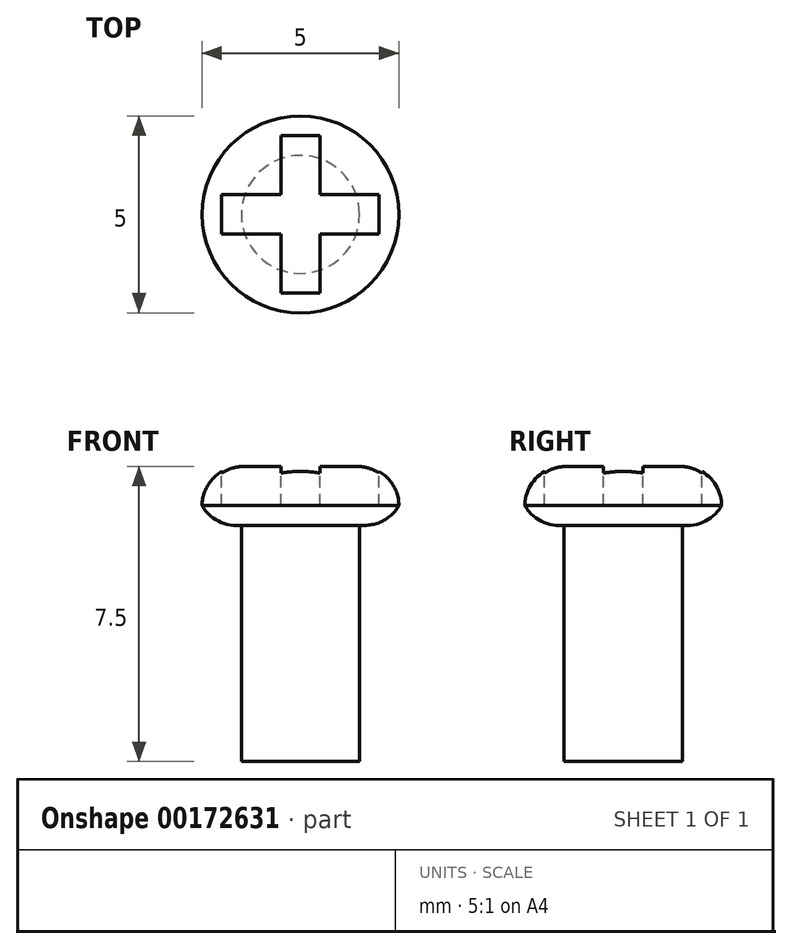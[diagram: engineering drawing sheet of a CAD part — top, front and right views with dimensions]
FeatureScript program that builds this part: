
annotation { "Feature Type Name" : "Feature", "Feature Type Description" : "" }
export const myFeature = defineFeature(function(context is Context, id is Id, definition is map)
    precondition{}
    {
        {
            var Q0;
            Q0=qCreatedBy(makeId("Top.planeOp"),FACE);
            var sketch = newSketch(context, id + "F0", { "sketchPlane" : qUnion([Q0])});
            skCircle(sketch, "E0", {"center": v(0, 0) * mm, "radius": 1.5 * mm});
            skSolve(sketch);
        }
        {
            var Q0;
            Q0 = qSketchRegion(id + "F0", true);
            extrude(context, id + "F1", {"entities" : qUnion([Q0]), "depth" : 6 * mm});
        }
        {
            var Q0;
            Q0=makeQuery(id+"F1.opExtrude","CAP_FACE",FACE,{"disambiguationData":[OSD([sQuery(id+"F0.wireOp",EDGE,"E0")])],"isStart":false});
            var sketch = newSketch(context, id + "F2", { "sketchPlane" : qUnion([Q0])});
            skCircle(sketch, "E1", {"center": v(0, 0) * mm, "radius": 2.5 * mm});
            skSolve(sketch);
        }
        {
            var Q0;
            Q0 = qSketchRegion(id + "F2", true);
            extrude(context, id + "F3", {"entities" : qUnion([Q0]), "operationType" : NewBodyOperationType.ADD, "depth" : 1.5 * mm});
        }
        {
            var Q0;
            Q0=makeQuery(id+"F3.opExtrude","CAP_FACE",FACE,{"disambiguationData":[OSD([sQuery(id+"F2.wireOp",EDGE,"E1")])],"isStart":false});
            var sketch = newSketch(context, id + "F4", { "sketchPlane" : qUnion([Q0])});
            skLineSegment(sketch, "E2.bottom", {"start": v(-0.5, 2) * mm, "end": v(0.5, 2) * mm});
            skLineSegment(sketch, "E2.top", {"start": v(-0.5, -2) * mm, "end": v(0.5, -2) * mm});
            skLineSegment(sketch, "E2.left", {"start": v(-0.5, 2) * mm, "end": v(-0.5, -2) * mm});
            skLineSegment(sketch, "E2.right", {"start": v(0.5, 2) * mm, "end": v(0.5, -2) * mm});
            skPoint(sketch, "E2.middle", {"position": v(0, 0) * mm});
            skLineSegment(sketch, "E3.bottom", {"start": v(-2, 0.5) * mm, "end": v(2, 0.5) * mm});
            skLineSegment(sketch, "E3.top", {"start": v(-2, -0.5) * mm, "end": v(2, -0.5) * mm});
            skLineSegment(sketch, "E3.left", {"start": v(-2, 0.5) * mm, "end": v(-2, -0.5) * mm});
            skLineSegment(sketch, "E3.right", {"start": v(2, 0.5) * mm, "end": v(2, -0.5) * mm});
            skSolve(sketch);
        }
        {
            var Q0;
            Q0 = qSketchRegion(id + "F4", true);
            extrude(context, id + "F5", {"entities" : qUnion([Q0]), "operationType" : NewBodyOperationType.REMOVE, "oppositeDirection" : true, "depth" : 1 * mm});
        }
        {
            var Q0;
            Q0=makeQuery(id+"F3.opExtrude","CAP_EDGE",EDGE,{"disambiguationData":[OSD([sQuery(id+"F2.wireOp",EDGE,"E1")])],"isStart":false});
            fillet(context, id + "F6", {"entities" : qUnion([Q0]), "radius" : 1 * mm, "tangentPropagation" : true, "allowEdgeOverflow" : false});
        }
        {
            var Q0;
            Q0=makeQuery(id+"F3.opExtrude","CAP_EDGE",EDGE,{"disambiguationData":[OSD([sQuery(id+"F2.wireOp",EDGE,"E1")])],"isStart":true});
            fillet(context, id + "F7", {"entities" : qUnion([Q0]), "radius" : 1 * mm, "tangentPropagation" : true, "allowEdgeOverflow" : false});
        }
    });
